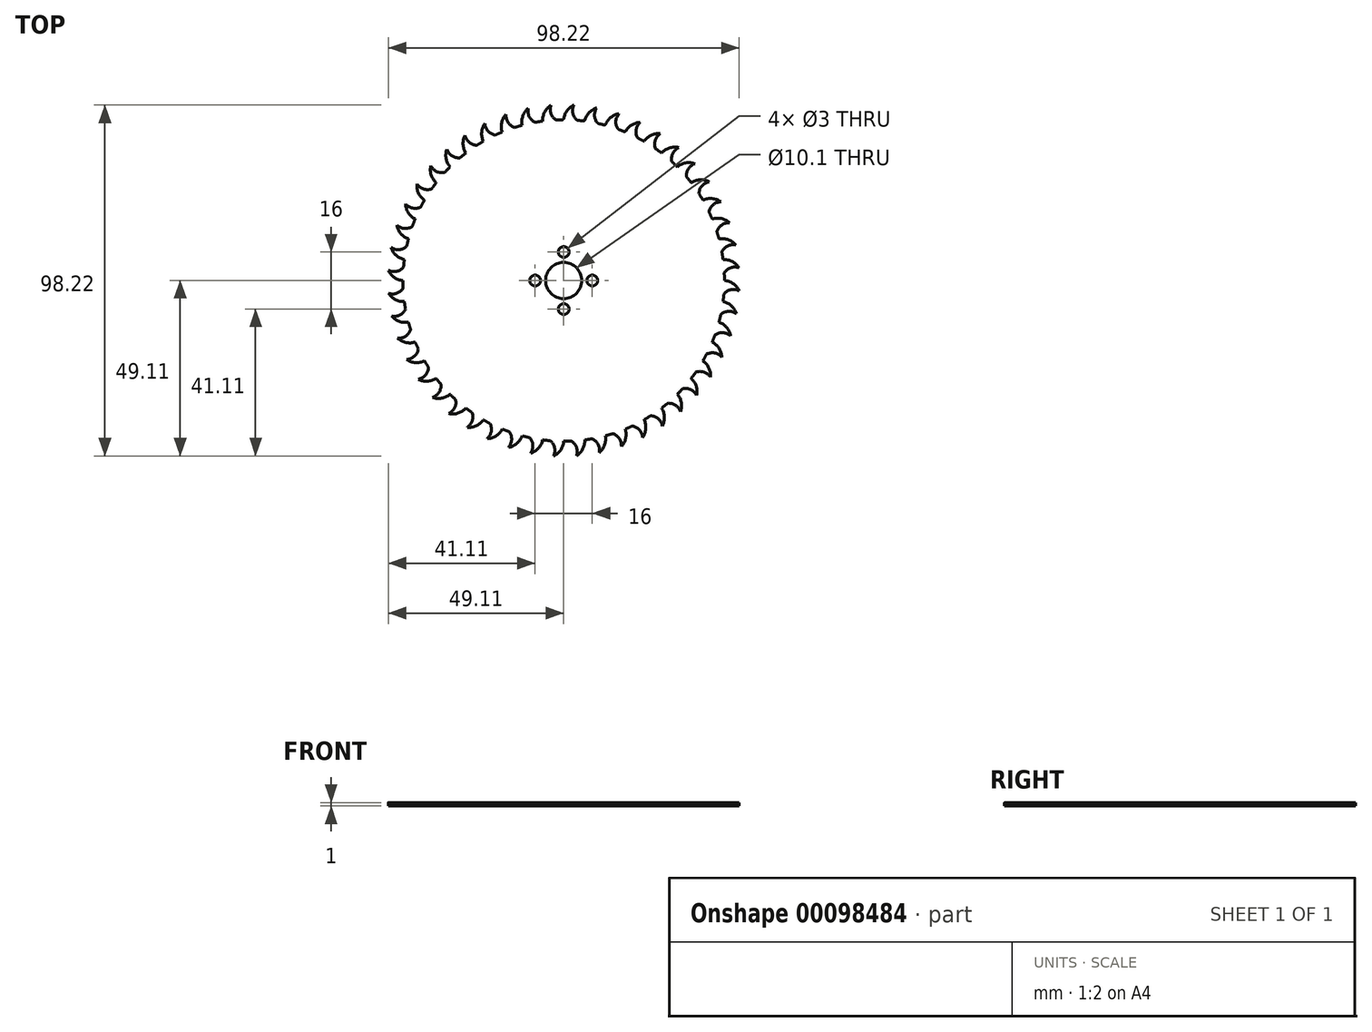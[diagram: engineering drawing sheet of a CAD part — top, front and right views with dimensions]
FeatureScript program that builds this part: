
annotation { "Feature Type Name" : "Feature", "Feature Type Description" : "" }
export const myFeature = defineFeature(function(context is Context, id is Id, definition is map)
    precondition{}
    {
        {
            var Q0;
            Q0=qCreatedBy(makeId("Top.planeOp"),FACE);
            var sketch = newSketch(context, id + "F0", { "sketchPlane" : qUnion([Q0])});
            skCircle(sketch, "E0", {"center": v(0, 0) * mm, "radius": 45 * mm, "construction": true});
            skArc(sketch, "E1", {"start": v(2.87, 49.11) * mm, "mid": v(1, 47.62) * mm, "end": v(0.05, 45.42) * mm});
            skArc(sketch, "E2", {"start": v(2.87, 49.11) * mm, "mid": v(2.52, 47.02) * mm, "end": v(3.45, 45.12) * mm});
            skArc(sketch, "E3.1.0", {"start": v(-3.57, 49.07) * mm, "mid": v(-5.33, 47.15) * mm, "end": v(-5.87, 44.62) * mm});
            skArc(sketch, "E3.1.1", {"start": v(-3.57, 49.07) * mm, "mid": v(-3.64, 46.95) * mm, "end": v(-2.47, 45.19) * mm});
            skArc(sketch, "E3.2.0", {"start": v(-9.94, 48.18) * mm, "mid": v(-11.44, 46.06) * mm, "end": v(-11.65, 43.47) * mm});
            skArc(sketch, "E3.2.1", {"start": v(-9.94, 48.18) * mm, "mid": v(-9.65, 45.9) * mm, "end": v(-8, 44.28) * mm});
            skArc(sketch, "E3.3.0", {"start": v(-16.15, 46.47) * mm, "mid": v(-17.35, 44.17) * mm, "end": v(-17.22, 41.57) * mm});
            skArc(sketch, "E3.3.1", {"start": v(-16.15, 46.47) * mm, "mid": v(-15.56, 44.24) * mm, "end": v(-13.7, 42.86) * mm});
            skArc(sketch, "E3.4.0", {"start": v(-22.07, 43.97) * mm, "mid": v(-22.97, 41.53) * mm, "end": v(-22.5, 38.97) * mm});
            skArc(sketch, "E3.4.1", {"start": v(-22.07, 43.97) * mm, "mid": v(-21.2, 41.83) * mm, "end": v(-19.18, 40.7) * mm});
            skArc(sketch, "E3.5.0", {"start": v(-27.62, 40.7) * mm, "mid": v(-28.2, 38.17) * mm, "end": v(-27.4, 35.7) * mm});
            skArc(sketch, "E3.5.1", {"start": v(-27.62, 40.7) * mm, "mid": v(-26.48, 38.7) * mm, "end": v(-24.33, 37.86) * mm});
            skArc(sketch, "E3.6.0", {"start": v(-32.7, 36.75) * mm, "mid": v(-32.93, 34.17) * mm, "end": v(-31.82, 31.82) * mm});
            skArc(sketch, "E3.6.1", {"start": v(-32.7, 36.75) * mm, "mid": v(-31.3, 34.92) * mm, "end": v(-29.06, 34.36) * mm});
            skArc(sketch, "E3.7.0", {"start": v(-37.22, 32.17) * mm, "mid": v(-37.11, 29.58) * mm, "end": v(-35.7, 27.4) * mm});
            skArc(sketch, "E3.7.1", {"start": v(-37.22, 32.17) * mm, "mid": v(-35.6, 30.53) * mm, "end": v(-33.3, 30.27) * mm});
            skArc(sketch, "E3.8.0", {"start": v(-41.1, 27.04) * mm, "mid": v(-40.65, 24.48) * mm, "end": v(-38.97, 22.5) * mm});
            skArc(sketch, "E3.8.1", {"start": v(-41.1, 27.04) * mm, "mid": v(-39.27, 25.63) * mm, "end": v(-36.96, 25.66) * mm});
            skArc(sketch, "E3.9.0", {"start": v(-44.28, 21.44) * mm, "mid": v(-43.5, 18.96) * mm, "end": v(-41.57, 17.22) * mm});
            skArc(sketch, "E3.9.1", {"start": v(-44.28, 21.44) * mm, "mid": v(-42.28, 20.28) * mm, "end": v(-40, 20.62) * mm});
            skArc(sketch, "E3.10.0", {"start": v(-46.7, 15.48) * mm, "mid": v(-45.6, 13.12) * mm, "end": v(-43.47, 11.65) * mm});
            skArc(sketch, "E3.10.1", {"start": v(-46.7, 15.48) * mm, "mid": v(-44.57, 14.59) * mm, "end": v(-42.35, 15.22) * mm});
            skArc(sketch, "E3.11.0", {"start": v(-48.32, 9.25) * mm, "mid": v(-46.93, 7.06) * mm, "end": v(-44.62, 5.87) * mm});
            skArc(sketch, "E3.11.1", {"start": v(-48.32, 9.25) * mm, "mid": v(-46.09, 8.65) * mm, "end": v(-43.97, 9.56) * mm});
            skArc(sketch, "E3.12.0", {"start": v(-49.11, 2.87) * mm, "mid": v(-47.45, 0.87) * mm, "end": v(-45, 0) * mm});
            skArc(sketch, "E3.12.1", {"start": v(-49.11, 2.87) * mm, "mid": v(-46.82, 2.56) * mm, "end": v(-44.84, 3.74) * mm});
            skArc(sketch, "E3.13.0", {"start": v(-49.07, -3.57) * mm, "mid": v(-47.15, -5.33) * mm, "end": v(-44.62, -5.87) * mm});
            skArc(sketch, "E3.13.1", {"start": v(-49.07, -3.57) * mm, "mid": v(-46.76, -3.58) * mm, "end": v(-44.95, -2.14) * mm});
            skArc(sketch, "E3.14.0", {"start": v(-48.18, -9.94) * mm, "mid": v(-46.06, -11.44) * mm, "end": v(-43.47, -11.65) * mm});
            skArc(sketch, "E3.14.1", {"start": v(-48.18, -9.94) * mm, "mid": v(-45.9, -9.65) * mm, "end": v(-44.28, -8) * mm});
            skArc(sketch, "E3.15.0", {"start": v(-46.47, -16.15) * mm, "mid": v(-44.17, -17.35) * mm, "end": v(-41.57, -17.22) * mm});
            skArc(sketch, "E3.15.1", {"start": v(-46.47, -16.15) * mm, "mid": v(-44.24, -15.56) * mm, "end": v(-42.86, -13.7) * mm});
            skArc(sketch, "E3.16.0", {"start": v(-43.97, -22.07) * mm, "mid": v(-41.53, -22.97) * mm, "end": v(-38.97, -22.5) * mm});
            skArc(sketch, "E3.16.1", {"start": v(-43.97, -22.07) * mm, "mid": v(-41.83, -21.2) * mm, "end": v(-40.7, -19.18) * mm});
            skArc(sketch, "E3.17.0", {"start": v(-40.7, -27.62) * mm, "mid": v(-38.17, -28.2) * mm, "end": v(-35.7, -27.4) * mm});
            skArc(sketch, "E3.17.1", {"start": v(-40.7, -27.62) * mm, "mid": v(-38.7, -26.48) * mm, "end": v(-37.86, -24.33) * mm});
            skArc(sketch, "E3.18.0", {"start": v(-36.75, -32.7) * mm, "mid": v(-34.17, -32.93) * mm, "end": v(-31.82, -31.82) * mm});
            skArc(sketch, "E3.18.1", {"start": v(-36.75, -32.7) * mm, "mid": v(-34.92, -31.3) * mm, "end": v(-34.36, -29.06) * mm});
            skArc(sketch, "E3.19.0", {"start": v(-32.17, -37.22) * mm, "mid": v(-29.58, -37.11) * mm, "end": v(-27.4, -35.7) * mm});
            skArc(sketch, "E3.19.1", {"start": v(-32.17, -37.22) * mm, "mid": v(-30.53, -35.6) * mm, "end": v(-30.27, -33.3) * mm});
            skArc(sketch, "E3.20.0", {"start": v(-27.04, -41.1) * mm, "mid": v(-24.48, -40.65) * mm, "end": v(-22.5, -38.97) * mm});
            skArc(sketch, "E3.20.1", {"start": v(-27.04, -41.1) * mm, "mid": v(-25.63, -39.27) * mm, "end": v(-25.66, -36.96) * mm});
            skArc(sketch, "E3.21.0", {"start": v(-21.44, -44.28) * mm, "mid": v(-18.96, -43.5) * mm, "end": v(-17.22, -41.57) * mm});
            skArc(sketch, "E3.21.1", {"start": v(-21.44, -44.28) * mm, "mid": v(-20.28, -42.28) * mm, "end": v(-20.62, -40) * mm});
            skArc(sketch, "E3.22.0", {"start": v(-15.48, -46.7) * mm, "mid": v(-13.12, -45.6) * mm, "end": v(-11.65, -43.47) * mm});
            skArc(sketch, "E3.22.1", {"start": v(-15.48, -46.7) * mm, "mid": v(-14.59, -44.57) * mm, "end": v(-15.22, -42.35) * mm});
            skArc(sketch, "E3.23.0", {"start": v(-9.25, -48.32) * mm, "mid": v(-7.06, -46.93) * mm, "end": v(-5.87, -44.62) * mm});
            skArc(sketch, "E3.23.1", {"start": v(-9.25, -48.32) * mm, "mid": v(-8.65, -46.09) * mm, "end": v(-9.56, -43.97) * mm});
            skArc(sketch, "E3.24.0", {"start": v(-2.87, -49.11) * mm, "mid": v(-0.87, -47.45) * mm, "end": v(0, -45) * mm});
            skArc(sketch, "E3.24.1", {"start": v(-2.87, -49.11) * mm, "mid": v(-2.56, -46.82) * mm, "end": v(-3.74, -44.84) * mm});
            skArc(sketch, "E3.25.0", {"start": v(3.57, -49.07) * mm, "mid": v(5.33, -47.15) * mm, "end": v(5.87, -44.62) * mm});
            skArc(sketch, "E3.25.1", {"start": v(3.57, -49.07) * mm, "mid": v(3.58, -46.76) * mm, "end": v(2.14, -44.95) * mm});
            skArc(sketch, "E3.26.0", {"start": v(9.94, -48.18) * mm, "mid": v(11.44, -46.06) * mm, "end": v(11.65, -43.47) * mm});
            skArc(sketch, "E3.26.1", {"start": v(9.94, -48.18) * mm, "mid": v(9.65, -45.9) * mm, "end": v(8, -44.28) * mm});
            skArc(sketch, "E3.27.0", {"start": v(16.15, -46.47) * mm, "mid": v(17.35, -44.17) * mm, "end": v(17.22, -41.57) * mm});
            skArc(sketch, "E3.27.1", {"start": v(16.15, -46.47) * mm, "mid": v(15.56, -44.24) * mm, "end": v(13.7, -42.86) * mm});
            skArc(sketch, "E3.28.0", {"start": v(22.07, -43.97) * mm, "mid": v(22.97, -41.53) * mm, "end": v(22.5, -38.97) * mm});
            skArc(sketch, "E3.28.1", {"start": v(22.07, -43.97) * mm, "mid": v(21.2, -41.83) * mm, "end": v(19.18, -40.7) * mm});
            skArc(sketch, "E3.29.0", {"start": v(27.62, -40.7) * mm, "mid": v(28.2, -38.17) * mm, "end": v(27.4, -35.7) * mm});
            skArc(sketch, "E3.29.1", {"start": v(27.62, -40.7) * mm, "mid": v(26.48, -38.7) * mm, "end": v(24.33, -37.86) * mm});
            skArc(sketch, "E3.30.0", {"start": v(32.7, -36.75) * mm, "mid": v(32.93, -34.17) * mm, "end": v(31.82, -31.82) * mm});
            skArc(sketch, "E3.30.1", {"start": v(32.7, -36.75) * mm, "mid": v(31.3, -34.92) * mm, "end": v(29.06, -34.36) * mm});
            skArc(sketch, "E3.31.0", {"start": v(37.22, -32.17) * mm, "mid": v(37.11, -29.58) * mm, "end": v(35.7, -27.4) * mm});
            skArc(sketch, "E3.31.1", {"start": v(37.22, -32.17) * mm, "mid": v(35.6, -30.53) * mm, "end": v(33.3, -30.27) * mm});
            skArc(sketch, "E3.32.0", {"start": v(41.1, -27.04) * mm, "mid": v(40.65, -24.48) * mm, "end": v(38.97, -22.5) * mm});
            skArc(sketch, "E3.32.1", {"start": v(41.1, -27.04) * mm, "mid": v(39.27, -25.63) * mm, "end": v(36.96, -25.66) * mm});
            skArc(sketch, "E3.33.0", {"start": v(44.28, -21.44) * mm, "mid": v(43.5, -18.96) * mm, "end": v(41.57, -17.22) * mm});
            skArc(sketch, "E3.33.1", {"start": v(44.28, -21.44) * mm, "mid": v(42.28, -20.28) * mm, "end": v(40, -20.62) * mm});
            skArc(sketch, "E3.34.0", {"start": v(46.7, -15.48) * mm, "mid": v(45.6, -13.12) * mm, "end": v(43.47, -11.65) * mm});
            skArc(sketch, "E3.34.1", {"start": v(46.7, -15.48) * mm, "mid": v(44.57, -14.59) * mm, "end": v(42.35, -15.22) * mm});
            skArc(sketch, "E3.35.0", {"start": v(48.32, -9.25) * mm, "mid": v(46.93, -7.06) * mm, "end": v(44.62, -5.87) * mm});
            skArc(sketch, "E3.35.1", {"start": v(48.32, -9.25) * mm, "mid": v(46.09, -8.65) * mm, "end": v(43.97, -9.56) * mm});
            skArc(sketch, "E3.36.0", {"start": v(49.11, -2.87) * mm, "mid": v(47.45, -0.87) * mm, "end": v(45, 0) * mm});
            skArc(sketch, "E3.36.1", {"start": v(49.11, -2.87) * mm, "mid": v(46.82, -2.56) * mm, "end": v(44.84, -3.74) * mm});
            skArc(sketch, "E3.37.0", {"start": v(49.07, 3.57) * mm, "mid": v(47.15, 5.33) * mm, "end": v(44.62, 5.87) * mm});
            skArc(sketch, "E3.37.1", {"start": v(49.07, 3.57) * mm, "mid": v(46.76, 3.58) * mm, "end": v(44.95, 2.14) * mm});
            skArc(sketch, "E3.38.0", {"start": v(48.18, 9.94) * mm, "mid": v(46.06, 11.44) * mm, "end": v(43.47, 11.65) * mm});
            skArc(sketch, "E3.38.1", {"start": v(48.18, 9.94) * mm, "mid": v(45.9, 9.65) * mm, "end": v(44.28, 8) * mm});
            skArc(sketch, "E3.39.0", {"start": v(46.47, 16.15) * mm, "mid": v(44.17, 17.35) * mm, "end": v(41.57, 17.22) * mm});
            skArc(sketch, "E3.39.1", {"start": v(46.47, 16.15) * mm, "mid": v(44.24, 15.56) * mm, "end": v(42.86, 13.7) * mm});
            skArc(sketch, "E3.40.0", {"start": v(43.97, 22.07) * mm, "mid": v(41.53, 22.97) * mm, "end": v(38.97, 22.5) * mm});
            skArc(sketch, "E3.40.1", {"start": v(43.97, 22.07) * mm, "mid": v(41.83, 21.2) * mm, "end": v(40.7, 19.18) * mm});
            skArc(sketch, "E3.41.0", {"start": v(40.7, 27.62) * mm, "mid": v(38.17, 28.2) * mm, "end": v(35.7, 27.4) * mm});
            skArc(sketch, "E3.41.1", {"start": v(40.7, 27.62) * mm, "mid": v(38.7, 26.48) * mm, "end": v(37.86, 24.33) * mm});
            skArc(sketch, "E3.42.0", {"start": v(36.75, 32.7) * mm, "mid": v(34.17, 32.93) * mm, "end": v(31.82, 31.82) * mm});
            skArc(sketch, "E3.42.1", {"start": v(36.75, 32.7) * mm, "mid": v(34.92, 31.3) * mm, "end": v(34.36, 29.06) * mm});
            skArc(sketch, "E3.43.0", {"start": v(32.17, 37.22) * mm, "mid": v(29.58, 37.11) * mm, "end": v(27.4, 35.7) * mm});
            skArc(sketch, "E3.43.1", {"start": v(32.17, 37.22) * mm, "mid": v(30.53, 35.6) * mm, "end": v(30.27, 33.3) * mm});
            skArc(sketch, "E3.44.0", {"start": v(27.04, 41.1) * mm, "mid": v(24.48, 40.65) * mm, "end": v(22.5, 38.97) * mm});
            skArc(sketch, "E3.44.1", {"start": v(27.04, 41.1) * mm, "mid": v(25.63, 39.27) * mm, "end": v(25.66, 36.96) * mm});
            skArc(sketch, "E3.45.0", {"start": v(21.44, 44.28) * mm, "mid": v(19.14, 43.61) * mm, "end": v(17.43, 41.94) * mm});
            skArc(sketch, "E3.45.1", {"start": v(21.44, 44.28) * mm, "mid": v(20.28, 42.28) * mm, "end": v(20.62, 40) * mm});
            skArc(sketch, "E3.46.0", {"start": v(15.48, 46.7) * mm, "mid": v(13.29, 45.74) * mm, "end": v(11.8, 43.86) * mm});
            skArc(sketch, "E3.46.1", {"start": v(15.48, 46.7) * mm, "mid": v(14.6, 44.77) * mm, "end": v(15, 42.7) * mm});
            skArc(sketch, "E3.47.0", {"start": v(9.25, 48.32) * mm, "mid": v(7.2, 47.08) * mm, "end": v(5.98, 45.02) * mm});
            skArc(sketch, "E3.47.1", {"start": v(9.25, 48.32) * mm, "mid": v(8.64, 46.3) * mm, "end": v(9.3, 44.29) * mm});
            skArc(sketch, "E4", {"start": v(4.08, 44.81) * mm, "mid": v(4.76, 44.75) * mm, "end": v(5.44, 44.67) * mm});
            skArc(sketch, "E5.1.0", {"start": v(-1.8, 44.96) * mm, "mid": v(-1.12, 44.99) * mm, "end": v(-0.44, 45) * mm});
            skArc(sketch, "E5.2.0", {"start": v(-8, 44.28) * mm, "mid": v(-6.93, 44.46) * mm, "end": v(-5.87, 44.62) * mm});
            skArc(sketch, "E5.3.0", {"start": v(-13.7, 42.86) * mm, "mid": v(-12.68, 43.18) * mm, "end": v(-11.65, 43.47) * mm});
            skArc(sketch, "E5.4.0", {"start": v(-19.18, 40.7) * mm, "mid": v(-18.2, 41.15) * mm, "end": v(-17.22, 41.57) * mm});
            skArc(sketch, "E5.5.0", {"start": v(-24.33, 37.86) * mm, "mid": v(-23.42, 38.42) * mm, "end": v(-22.5, 38.97) * mm});
            skArc(sketch, "E5.6.0", {"start": v(-29.06, 34.36) * mm, "mid": v(-28.24, 35.04) * mm, "end": v(-27.4, 35.7) * mm});
            skArc(sketch, "E5.7.0", {"start": v(-33.3, 30.27) * mm, "mid": v(-32.57, 31.05) * mm, "end": v(-31.82, 31.82) * mm});
            skArc(sketch, "E5.8.0", {"start": v(-36.96, 25.66) * mm, "mid": v(-36.34, 26.54) * mm, "end": v(-35.7, 27.4) * mm});
            skArc(sketch, "E5.9.0", {"start": v(-40, 20.62) * mm, "mid": v(-39.5, 21.57) * mm, "end": v(-38.97, 22.5) * mm});
            skArc(sketch, "E5.10.0", {"start": v(-42.35, 15.22) * mm, "mid": v(-41.97, 16.23) * mm, "end": v(-41.57, 17.22) * mm});
            skArc(sketch, "E5.11.0", {"start": v(-43.97, 9.56) * mm, "mid": v(-43.73, 10.6) * mm, "end": v(-43.47, 11.65) * mm});
            skArc(sketch, "E5.12.0", {"start": v(-44.84, 3.74) * mm, "mid": v(-44.74, 4.8) * mm, "end": v(-44.62, 5.87) * mm});
            skArc(sketch, "E5.13.0", {"start": v(-44.95, -2.14) * mm, "mid": v(-44.99, -1.07) * mm, "end": v(-45, 0) * mm});
            skArc(sketch, "E5.14.0", {"start": v(-44.28, -8) * mm, "mid": v(-44.46, -6.93) * mm, "end": v(-44.62, -5.87) * mm});
            skArc(sketch, "E5.15.0", {"start": v(-42.86, -13.7) * mm, "mid": v(-43.18, -12.68) * mm, "end": v(-43.47, -11.65) * mm});
            skArc(sketch, "E5.16.0", {"start": v(-40.7, -19.18) * mm, "mid": v(-41.15, -18.2) * mm, "end": v(-41.57, -17.22) * mm});
            skArc(sketch, "E5.17.0", {"start": v(-37.86, -24.33) * mm, "mid": v(-38.42, -23.42) * mm, "end": v(-38.97, -22.5) * mm});
            skArc(sketch, "E5.18.0", {"start": v(-34.36, -29.06) * mm, "mid": v(-35.04, -28.24) * mm, "end": v(-35.7, -27.4) * mm});
            skArc(sketch, "E5.19.0", {"start": v(-30.27, -33.3) * mm, "mid": v(-31.05, -32.57) * mm, "end": v(-31.82, -31.82) * mm});
            skArc(sketch, "E5.20.0", {"start": v(-25.66, -36.96) * mm, "mid": v(-26.54, -36.34) * mm, "end": v(-27.4, -35.7) * mm});
            skArc(sketch, "E5.21.0", {"start": v(-20.62, -40) * mm, "mid": v(-21.57, -39.5) * mm, "end": v(-22.5, -38.97) * mm});
            skArc(sketch, "E5.22.0", {"start": v(-15.22, -42.35) * mm, "mid": v(-16.23, -41.97) * mm, "end": v(-17.22, -41.57) * mm});
            skArc(sketch, "E5.23.0", {"start": v(-9.56, -43.97) * mm, "mid": v(-10.6, -43.73) * mm, "end": v(-11.65, -43.47) * mm});
            skArc(sketch, "E5.24.0", {"start": v(-3.74, -44.84) * mm, "mid": v(-4.8, -44.74) * mm, "end": v(-5.87, -44.62) * mm});
            skArc(sketch, "E5.25.0", {"start": v(2.14, -44.95) * mm, "mid": v(1.07, -44.99) * mm, "end": v(0, -45) * mm});
            skArc(sketch, "E5.26.0", {"start": v(8, -44.28) * mm, "mid": v(6.93, -44.46) * mm, "end": v(5.87, -44.62) * mm});
            skArc(sketch, "E5.27.0", {"start": v(13.7, -42.86) * mm, "mid": v(12.68, -43.18) * mm, "end": v(11.65, -43.47) * mm});
            skArc(sketch, "E5.28.0", {"start": v(19.18, -40.7) * mm, "mid": v(18.2, -41.15) * mm, "end": v(17.22, -41.57) * mm});
            skArc(sketch, "E5.29.0", {"start": v(24.33, -37.86) * mm, "mid": v(23.42, -38.42) * mm, "end": v(22.5, -38.97) * mm});
            skArc(sketch, "E5.30.0", {"start": v(29.06, -34.36) * mm, "mid": v(28.24, -35.04) * mm, "end": v(27.4, -35.7) * mm});
            skArc(sketch, "E5.31.0", {"start": v(33.3, -30.27) * mm, "mid": v(32.57, -31.05) * mm, "end": v(31.82, -31.82) * mm});
            skArc(sketch, "E5.32.0", {"start": v(36.96, -25.66) * mm, "mid": v(36.34, -26.54) * mm, "end": v(35.7, -27.4) * mm});
            skArc(sketch, "E5.33.0", {"start": v(40, -20.62) * mm, "mid": v(39.5, -21.57) * mm, "end": v(38.97, -22.5) * mm});
            skArc(sketch, "E5.34.0", {"start": v(42.35, -15.22) * mm, "mid": v(41.97, -16.23) * mm, "end": v(41.57, -17.22) * mm});
            skArc(sketch, "E5.35.0", {"start": v(43.97, -9.56) * mm, "mid": v(43.73, -10.6) * mm, "end": v(43.47, -11.65) * mm});
            skArc(sketch, "E5.36.0", {"start": v(44.84, -3.74) * mm, "mid": v(44.74, -4.8) * mm, "end": v(44.62, -5.87) * mm});
            skArc(sketch, "E5.37.0", {"start": v(44.95, 2.14) * mm, "mid": v(44.99, 1.07) * mm, "end": v(45, 0) * mm});
            skArc(sketch, "E5.38.0", {"start": v(44.28, 8) * mm, "mid": v(44.46, 6.93) * mm, "end": v(44.62, 5.87) * mm});
            skArc(sketch, "E5.39.0", {"start": v(42.86, 13.7) * mm, "mid": v(43.18, 12.68) * mm, "end": v(43.47, 11.65) * mm});
            skArc(sketch, "E5.40.0", {"start": v(40.7, 19.18) * mm, "mid": v(41.15, 18.2) * mm, "end": v(41.57, 17.22) * mm});
            skArc(sketch, "E5.41.0", {"start": v(37.86, 24.33) * mm, "mid": v(38.42, 23.42) * mm, "end": v(38.97, 22.5) * mm});
            skArc(sketch, "E5.42.0", {"start": v(34.36, 29.06) * mm, "mid": v(35.04, 28.24) * mm, "end": v(35.7, 27.4) * mm});
            skArc(sketch, "E5.43.0", {"start": v(30.27, 33.3) * mm, "mid": v(31.05, 32.57) * mm, "end": v(31.82, 31.82) * mm});
            skArc(sketch, "E5.44.0", {"start": v(25.66, 36.96) * mm, "mid": v(26.54, 36.34) * mm, "end": v(27.4, 35.7) * mm});
            skArc(sketch, "E5.45.0", {"start": v(20.62, 40) * mm, "mid": v(21.57, 39.5) * mm, "end": v(22.5, 38.97) * mm});
            skArc(sketch, "E5.46.0", {"start": v(15.54, 42.23) * mm, "mid": v(16.18, 42) * mm, "end": v(16.81, 41.74) * mm});
            skArc(sketch, "E5.47.0", {"start": v(9.9, 43.9) * mm, "mid": v(10.56, 43.74) * mm, "end": v(11.22, 43.58) * mm});
            skPoint(sketch, "E6.visualSharp", {"position": v(9.56, 43.97) * mm});
            skArc(sketch, "E6.filletArc", {"start": v(9.3, 44.29) * mm, "mid": v(9.57, 44.04) * mm, "end": v(9.9, 43.9) * mm});
            skPoint(sketch, "E7.visualSharp", {"position": v(11.65, 43.47) * mm});
            skArc(sketch, "E7.filletArc", {"start": v(11.22, 43.58) * mm, "mid": v(11.56, 43.61) * mm, "end": v(11.8, 43.86) * mm});
            skPoint(sketch, "E8.visualSharp", {"position": v(3.74, 44.84) * mm});
            skArc(sketch, "E8.filletArc", {"start": v(3.45, 45.12) * mm, "mid": v(3.74, 44.91) * mm, "end": v(4.08, 44.81) * mm});
            skPoint(sketch, "E9.visualSharp", {"position": v(-2.14, 44.95) * mm});
            skArc(sketch, "E9.filletArc", {"start": v(-2.47, 45.19) * mm, "mid": v(-2.16, 45.01) * mm, "end": v(-1.8, 44.96) * mm});
            skPoint(sketch, "E10.visualSharp", {"position": v(0, 45) * mm});
            skArc(sketch, "E10.filletArc", {"start": v(-0.44, 45) * mm, "mid": v(-0.12, 45.12) * mm, "end": v(0.05, 45.42) * mm});
            skPoint(sketch, "E11.visualSharp", {"position": v(5.87, 44.62) * mm});
            skArc(sketch, "E11.filletArc", {"start": v(5.44, 44.67) * mm, "mid": v(5.77, 44.75) * mm, "end": v(5.98, 45.02) * mm});
            skPoint(sketch, "E12.visualSharp", {"position": v(17.22, 41.57) * mm});
            skArc(sketch, "E12.filletArc", {"start": v(16.81, 41.74) * mm, "mid": v(17.16, 41.73) * mm, "end": v(17.43, 41.94) * mm});
            skPoint(sketch, "E13.visualSharp", {"position": v(15.22, 42.35) * mm});
            skArc(sketch, "E13.filletArc", {"start": v(15, 42.7) * mm, "mid": v(15.23, 42.41) * mm, "end": v(15.54, 42.23) * mm});
            skCircle(sketch, "E14", {"center": v(0, 0) * mm, "radius": 5.05 * mm});
            skSolve(sketch);
        }
        {
            var Q0;
            Q0=qSketchRegion(id+"F0",true);
            extrude(context, id + "F1", {"entities" : qUnion([Q0]), "depth" : 1 * mm});
        }
        {
            var Q0;
            Q0=makeQuery(id+"F1.opExtrude","CAP_FACE",FACE,{"disambiguationData":[OSD([sQuery(id+"F0.wireOp",EDGE,"E1"),sQuery(id+"F0.wireOp",EDGE,"E2"),sQuery(id+"F0.wireOp",EDGE,"E3.1.0"),sQuery(id+"F0.wireOp",EDGE,"E3.1.1"),sQuery(id+"F0.wireOp",EDGE,"E3.2.0"),sQuery(id+"F0.wireOp",EDGE,"E3.2.1"),sQuery(id+"F0.wireOp",EDGE,"E3.3.0"),sQuery(id+"F0.wireOp",EDGE,"E3.3.1"),sQuery(id+"F0.wireOp",EDGE,"E3.4.0"),sQuery(id+"F0.wireOp",EDGE,"E3.4.1"),sQuery(id+"F0.wireOp",EDGE,"E3.5.0"),sQuery(id+"F0.wireOp",EDGE,"E3.5.1"),sQuery(id+"F0.wireOp",EDGE,"E3.6.0"),sQuery(id+"F0.wireOp",EDGE,"E3.6.1"),sQuery(id+"F0.wireOp",EDGE,"E3.7.0"),sQuery(id+"F0.wireOp",EDGE,"E3.7.1"),sQuery(id+"F0.wireOp",EDGE,"E3.8.0"),sQuery(id+"F0.wireOp",EDGE,"E3.8.1"),sQuery(id+"F0.wireOp",EDGE,"E3.9.0"),sQuery(id+"F0.wireOp",EDGE,"E3.9.1"),sQuery(id+"F0.wireOp",EDGE,"E3.10.0"),sQuery(id+"F0.wireOp",EDGE,"E3.10.1"),sQuery(id+"F0.wireOp",EDGE,"E3.11.0"),sQuery(id+"F0.wireOp",EDGE,"E3.11.1"),sQuery(id+"F0.wireOp",EDGE,"E3.12.0"),sQuery(id+"F0.wireOp",EDGE,"E3.12.1"),sQuery(id+"F0.wireOp",EDGE,"E3.13.0"),sQuery(id+"F0.wireOp",EDGE,"E3.13.1"),sQuery(id+"F0.wireOp",EDGE,"E3.14.0"),sQuery(id+"F0.wireOp",EDGE,"E3.14.1"),sQuery(id+"F0.wireOp",EDGE,"E3.15.0"),sQuery(id+"F0.wireOp",EDGE,"E3.15.1"),sQuery(id+"F0.wireOp",EDGE,"E3.16.0"),sQuery(id+"F0.wireOp",EDGE,"E3.16.1"),sQuery(id+"F0.wireOp",EDGE,"E3.17.0"),sQuery(id+"F0.wireOp",EDGE,"E3.17.1"),sQuery(id+"F0.wireOp",EDGE,"E3.18.0"),sQuery(id+"F0.wireOp",EDGE,"E3.18.1"),sQuery(id+"F0.wireOp",EDGE,"E3.19.0"),sQuery(id+"F0.wireOp",EDGE,"E3.19.1"),sQuery(id+"F0.wireOp",EDGE,"E3.20.0"),sQuery(id+"F0.wireOp",EDGE,"E3.20.1"),sQuery(id+"F0.wireOp",EDGE,"E3.21.0"),sQuery(id+"F0.wireOp",EDGE,"E3.21.1"),sQuery(id+"F0.wireOp",EDGE,"E3.22.0"),sQuery(id+"F0.wireOp",EDGE,"E3.22.1"),sQuery(id+"F0.wireOp",EDGE,"E3.23.0"),sQuery(id+"F0.wireOp",EDGE,"E3.23.1"),sQuery(id+"F0.wireOp",EDGE,"E3.24.0"),sQuery(id+"F0.wireOp",EDGE,"E3.24.1"),sQuery(id+"F0.wireOp",EDGE,"E3.25.0"),sQuery(id+"F0.wireOp",EDGE,"E3.25.1"),sQuery(id+"F0.wireOp",EDGE,"E3.26.0"),sQuery(id+"F0.wireOp",EDGE,"E3.26.1"),sQuery(id+"F0.wireOp",EDGE,"E3.27.0"),sQuery(id+"F0.wireOp",EDGE,"E3.27.1"),sQuery(id+"F0.wireOp",EDGE,"E3.28.0"),sQuery(id+"F0.wireOp",EDGE,"E3.28.1"),sQuery(id+"F0.wireOp",EDGE,"E3.29.0"),sQuery(id+"F0.wireOp",EDGE,"E3.29.1"),sQuery(id+"F0.wireOp",EDGE,"E3.30.0"),sQuery(id+"F0.wireOp",EDGE,"E3.30.1"),sQuery(id+"F0.wireOp",EDGE,"E3.31.0"),sQuery(id+"F0.wireOp",EDGE,"E3.31.1"),sQuery(id+"F0.wireOp",EDGE,"E3.32.0"),sQuery(id+"F0.wireOp",EDGE,"E3.32.1"),sQuery(id+"F0.wireOp",EDGE,"E3.33.0"),sQuery(id+"F0.wireOp",EDGE,"E3.33.1"),sQuery(id+"F0.wireOp",EDGE,"E3.34.0"),sQuery(id+"F0.wireOp",EDGE,"E3.34.1"),sQuery(id+"F0.wireOp",EDGE,"E3.35.0"),sQuery(id+"F0.wireOp",EDGE,"E3.35.1"),sQuery(id+"F0.wireOp",EDGE,"E3.36.0"),sQuery(id+"F0.wireOp",EDGE,"E3.36.1"),sQuery(id+"F0.wireOp",EDGE,"E3.37.0"),sQuery(id+"F0.wireOp",EDGE,"E3.37.1"),sQuery(id+"F0.wireOp",EDGE,"E3.38.0"),sQuery(id+"F0.wireOp",EDGE,"E3.38.1"),sQuery(id+"F0.wireOp",EDGE,"E3.39.0"),sQuery(id+"F0.wireOp",EDGE,"E3.39.1"),sQuery(id+"F0.wireOp",EDGE,"E3.40.0"),sQuery(id+"F0.wireOp",EDGE,"E3.40.1"),sQuery(id+"F0.wireOp",EDGE,"E3.41.0"),sQuery(id+"F0.wireOp",EDGE,"E3.41.1"),sQuery(id+"F0.wireOp",EDGE,"E3.42.0"),sQuery(id+"F0.wireOp",EDGE,"E3.42.1"),sQuery(id+"F0.wireOp",EDGE,"E3.43.0"),sQuery(id+"F0.wireOp",EDGE,"E3.43.1"),sQuery(id+"F0.wireOp",EDGE,"E3.44.0"),sQuery(id+"F0.wireOp",EDGE,"E3.44.1"),sQuery(id+"F0.wireOp",EDGE,"E3.45.0"),sQuery(id+"F0.wireOp",EDGE,"E3.45.1"),sQuery(id+"F0.wireOp",EDGE,"E3.46.0"),sQuery(id+"F0.wireOp",EDGE,"E3.46.1"),sQuery(id+"F0.wireOp",EDGE,"E3.47.0"),sQuery(id+"F0.wireOp",EDGE,"E3.47.1"),sQuery(id+"F0.wireOp",EDGE,"E4"),sQuery(id+"F0.wireOp",EDGE,"E5.1.0"),sQuery(id+"F0.wireOp",EDGE,"E5.2.0"),sQuery(id+"F0.wireOp",EDGE,"E5.3.0"),sQuery(id+"F0.wireOp",EDGE,"E5.4.0"),sQuery(id+"F0.wireOp",EDGE,"E5.5.0"),sQuery(id+"F0.wireOp",EDGE,"E5.6.0"),sQuery(id+"F0.wireOp",EDGE,"E5.7.0"),sQuery(id+"F0.wireOp",EDGE,"E5.8.0"),sQuery(id+"F0.wireOp",EDGE,"E5.9.0"),sQuery(id+"F0.wireOp",EDGE,"E5.10.0"),sQuery(id+"F0.wireOp",EDGE,"E5.11.0"),sQuery(id+"F0.wireOp",EDGE,"E5.12.0"),sQuery(id+"F0.wireOp",EDGE,"E5.13.0"),sQuery(id+"F0.wireOp",EDGE,"E5.14.0"),sQuery(id+"F0.wireOp",EDGE,"E5.15.0"),sQuery(id+"F0.wireOp",EDGE,"E5.16.0"),sQuery(id+"F0.wireOp",EDGE,"E5.17.0"),sQuery(id+"F0.wireOp",EDGE,"E5.18.0"),sQuery(id+"F0.wireOp",EDGE,"E5.19.0"),sQuery(id+"F0.wireOp",EDGE,"E5.20.0"),sQuery(id+"F0.wireOp",EDGE,"E5.21.0"),sQuery(id+"F0.wireOp",EDGE,"E5.22.0"),sQuery(id+"F0.wireOp",EDGE,"E5.23.0"),sQuery(id+"F0.wireOp",EDGE,"E5.24.0"),sQuery(id+"F0.wireOp",EDGE,"E5.25.0"),sQuery(id+"F0.wireOp",EDGE,"E5.26.0"),sQuery(id+"F0.wireOp",EDGE,"E5.27.0"),sQuery(id+"F0.wireOp",EDGE,"E5.28.0"),sQuery(id+"F0.wireOp",EDGE,"E5.29.0"),sQuery(id+"F0.wireOp",EDGE,"E5.30.0"),sQuery(id+"F0.wireOp",EDGE,"E5.31.0"),sQuery(id+"F0.wireOp",EDGE,"E5.32.0"),sQuery(id+"F0.wireOp",EDGE,"E5.33.0"),sQuery(id+"F0.wireOp",EDGE,"E5.34.0"),sQuery(id+"F0.wireOp",EDGE,"E5.35.0"),sQuery(id+"F0.wireOp",EDGE,"E5.36.0"),sQuery(id+"F0.wireOp",EDGE,"E5.37.0"),sQuery(id+"F0.wireOp",EDGE,"E5.38.0"),sQuery(id+"F0.wireOp",EDGE,"E5.39.0"),sQuery(id+"F0.wireOp",EDGE,"E5.40.0"),sQuery(id+"F0.wireOp",EDGE,"E5.41.0"),sQuery(id+"F0.wireOp",EDGE,"E5.42.0"),sQuery(id+"F0.wireOp",EDGE,"E5.43.0"),sQuery(id+"F0.wireOp",EDGE,"E5.44.0"),sQuery(id+"F0.wireOp",EDGE,"E5.45.0"),sQuery(id+"F0.wireOp",EDGE,"E5.46.0"),sQuery(id+"F0.wireOp",EDGE,"E5.47.0"),sQuery(id+"F0.wireOp",EDGE,"E6.filletArc"),sQuery(id+"F0.wireOp",EDGE,"E7.filletArc"),sQuery(id+"F0.wireOp",EDGE,"E8.filletArc"),sQuery(id+"F0.wireOp",EDGE,"E9.filletArc"),sQuery(id+"F0.wireOp",EDGE,"E10.filletArc"),sQuery(id+"F0.wireOp",EDGE,"E11.filletArc"),sQuery(id+"F0.wireOp",EDGE,"E12.filletArc"),sQuery(id+"F0.wireOp",EDGE,"E13.filletArc"),sQuery(id+"F0.wireOp",EDGE,"E14")])],"isStart":false});
            var sketch = newSketch(context, id + "F2", { "sketchPlane" : qUnion([Q0])});
            skCircle(sketch, "E15", {"center": v(0, 0) * mm, "radius": 8 * mm, "construction": true});
            skPoint(sketch, "E16", {"position": v(0, 8) * mm});
            skPoint(sketch, "E17", {"position": v(-8, 0) * mm});
            skPoint(sketch, "E18", {"position": v(0, -8) * mm});
            skPoint(sketch, "E19", {"position": v(8, 0) * mm});
            skSolve(sketch);
        }
        {
            var Q0;
            Q0=sQuery(id+"F2.wireOp",VERTEX,"E16");
            var Q1;
            Q1=sQuery(id+"F2.wireOp",VERTEX,"E17");
            var Q2;
            Q2=sQuery(id+"F2.wireOp",VERTEX,"E18");
            var Q3;
            Q3=sQuery(id+"F2.wireOp",VERTEX,"E19");
            var Q4;
            Q4=makeQuery(id+"F1.opExtrude","SWEPT_BODY",BODY,{"disambiguationData":[OSD([sQuery(id+"F0.wireOp",EDGE,"E1"),sQuery(id+"F0.wireOp",EDGE,"E2"),sQuery(id+"F0.wireOp",EDGE,"E3.1.0"),sQuery(id+"F0.wireOp",EDGE,"E3.1.1"),sQuery(id+"F0.wireOp",EDGE,"E3.2.0"),sQuery(id+"F0.wireOp",EDGE,"E3.2.1"),sQuery(id+"F0.wireOp",EDGE,"E3.3.0"),sQuery(id+"F0.wireOp",EDGE,"E3.3.1"),sQuery(id+"F0.wireOp",EDGE,"E3.4.0"),sQuery(id+"F0.wireOp",EDGE,"E3.4.1"),sQuery(id+"F0.wireOp",EDGE,"E3.5.0"),sQuery(id+"F0.wireOp",EDGE,"E3.5.1"),sQuery(id+"F0.wireOp",EDGE,"E3.6.0"),sQuery(id+"F0.wireOp",EDGE,"E3.6.1"),sQuery(id+"F0.wireOp",EDGE,"E3.7.0"),sQuery(id+"F0.wireOp",EDGE,"E3.7.1"),sQuery(id+"F0.wireOp",EDGE,"E3.8.0"),sQuery(id+"F0.wireOp",EDGE,"E3.8.1"),sQuery(id+"F0.wireOp",EDGE,"E3.9.0"),sQuery(id+"F0.wireOp",EDGE,"E3.9.1"),sQuery(id+"F0.wireOp",EDGE,"E3.10.0"),sQuery(id+"F0.wireOp",EDGE,"E3.10.1"),sQuery(id+"F0.wireOp",EDGE,"E3.11.0"),sQuery(id+"F0.wireOp",EDGE,"E3.11.1"),sQuery(id+"F0.wireOp",EDGE,"E3.12.0"),sQuery(id+"F0.wireOp",EDGE,"E3.12.1"),sQuery(id+"F0.wireOp",EDGE,"E3.13.0"),sQuery(id+"F0.wireOp",EDGE,"E3.13.1"),sQuery(id+"F0.wireOp",EDGE,"E3.14.0"),sQuery(id+"F0.wireOp",EDGE,"E3.14.1"),sQuery(id+"F0.wireOp",EDGE,"E3.15.0"),sQuery(id+"F0.wireOp",EDGE,"E3.15.1"),sQuery(id+"F0.wireOp",EDGE,"E3.16.0"),sQuery(id+"F0.wireOp",EDGE,"E3.16.1"),sQuery(id+"F0.wireOp",EDGE,"E3.17.0"),sQuery(id+"F0.wireOp",EDGE,"E3.17.1"),sQuery(id+"F0.wireOp",EDGE,"E3.18.0"),sQuery(id+"F0.wireOp",EDGE,"E3.18.1"),sQuery(id+"F0.wireOp",EDGE,"E3.19.0"),sQuery(id+"F0.wireOp",EDGE,"E3.19.1"),sQuery(id+"F0.wireOp",EDGE,"E3.20.0"),sQuery(id+"F0.wireOp",EDGE,"E3.20.1"),sQuery(id+"F0.wireOp",EDGE,"E3.21.0"),sQuery(id+"F0.wireOp",EDGE,"E3.21.1"),sQuery(id+"F0.wireOp",EDGE,"E3.22.0"),sQuery(id+"F0.wireOp",EDGE,"E3.22.1"),sQuery(id+"F0.wireOp",EDGE,"E3.23.0"),sQuery(id+"F0.wireOp",EDGE,"E3.23.1"),sQuery(id+"F0.wireOp",EDGE,"E3.24.0"),sQuery(id+"F0.wireOp",EDGE,"E3.24.1"),sQuery(id+"F0.wireOp",EDGE,"E3.25.0"),sQuery(id+"F0.wireOp",EDGE,"E3.25.1"),sQuery(id+"F0.wireOp",EDGE,"E3.26.0"),sQuery(id+"F0.wireOp",EDGE,"E3.26.1"),sQuery(id+"F0.wireOp",EDGE,"E3.27.0"),sQuery(id+"F0.wireOp",EDGE,"E3.27.1"),sQuery(id+"F0.wireOp",EDGE,"E3.28.0"),sQuery(id+"F0.wireOp",EDGE,"E3.28.1"),sQuery(id+"F0.wireOp",EDGE,"E3.29.0"),sQuery(id+"F0.wireOp",EDGE,"E3.29.1"),sQuery(id+"F0.wireOp",EDGE,"E3.30.0"),sQuery(id+"F0.wireOp",EDGE,"E3.30.1"),sQuery(id+"F0.wireOp",EDGE,"E3.31.0"),sQuery(id+"F0.wireOp",EDGE,"E3.31.1"),sQuery(id+"F0.wireOp",EDGE,"E3.32.0"),sQuery(id+"F0.wireOp",EDGE,"E3.32.1"),sQuery(id+"F0.wireOp",EDGE,"E3.33.0"),sQuery(id+"F0.wireOp",EDGE,"E3.33.1"),sQuery(id+"F0.wireOp",EDGE,"E3.34.0"),sQuery(id+"F0.wireOp",EDGE,"E3.34.1"),sQuery(id+"F0.wireOp",EDGE,"E3.35.0"),sQuery(id+"F0.wireOp",EDGE,"E3.35.1"),sQuery(id+"F0.wireOp",EDGE,"E3.36.0"),sQuery(id+"F0.wireOp",EDGE,"E3.36.1"),sQuery(id+"F0.wireOp",EDGE,"E3.37.0"),sQuery(id+"F0.wireOp",EDGE,"E3.37.1"),sQuery(id+"F0.wireOp",EDGE,"E3.38.0"),sQuery(id+"F0.wireOp",EDGE,"E3.38.1"),sQuery(id+"F0.wireOp",EDGE,"E3.39.0"),sQuery(id+"F0.wireOp",EDGE,"E3.39.1"),sQuery(id+"F0.wireOp",EDGE,"E3.40.0"),sQuery(id+"F0.wireOp",EDGE,"E3.40.1"),sQuery(id+"F0.wireOp",EDGE,"E3.41.0"),sQuery(id+"F0.wireOp",EDGE,"E3.41.1"),sQuery(id+"F0.wireOp",EDGE,"E3.42.0"),sQuery(id+"F0.wireOp",EDGE,"E3.42.1"),sQuery(id+"F0.wireOp",EDGE,"E3.43.0"),sQuery(id+"F0.wireOp",EDGE,"E3.43.1"),sQuery(id+"F0.wireOp",EDGE,"E3.44.0"),sQuery(id+"F0.wireOp",EDGE,"E3.44.1"),sQuery(id+"F0.wireOp",EDGE,"E3.45.0"),sQuery(id+"F0.wireOp",EDGE,"E3.45.1"),sQuery(id+"F0.wireOp",EDGE,"E3.46.0"),sQuery(id+"F0.wireOp",EDGE,"E3.46.1"),sQuery(id+"F0.wireOp",EDGE,"E3.47.0"),sQuery(id+"F0.wireOp",EDGE,"E3.47.1"),sQuery(id+"F0.wireOp",EDGE,"E4"),sQuery(id+"F0.wireOp",EDGE,"E5.1.0"),sQuery(id+"F0.wireOp",EDGE,"E5.2.0"),sQuery(id+"F0.wireOp",EDGE,"E5.3.0"),sQuery(id+"F0.wireOp",EDGE,"E5.4.0"),sQuery(id+"F0.wireOp",EDGE,"E5.5.0"),sQuery(id+"F0.wireOp",EDGE,"E5.6.0"),sQuery(id+"F0.wireOp",EDGE,"E5.7.0"),sQuery(id+"F0.wireOp",EDGE,"E5.8.0"),sQuery(id+"F0.wireOp",EDGE,"E5.9.0"),sQuery(id+"F0.wireOp",EDGE,"E5.10.0"),sQuery(id+"F0.wireOp",EDGE,"E5.11.0"),sQuery(id+"F0.wireOp",EDGE,"E5.12.0"),sQuery(id+"F0.wireOp",EDGE,"E5.13.0"),sQuery(id+"F0.wireOp",EDGE,"E5.14.0"),sQuery(id+"F0.wireOp",EDGE,"E5.15.0"),sQuery(id+"F0.wireOp",EDGE,"E5.16.0"),sQuery(id+"F0.wireOp",EDGE,"E5.17.0"),sQuery(id+"F0.wireOp",EDGE,"E5.18.0"),sQuery(id+"F0.wireOp",EDGE,"E5.19.0"),sQuery(id+"F0.wireOp",EDGE,"E5.20.0"),sQuery(id+"F0.wireOp",EDGE,"E5.21.0"),sQuery(id+"F0.wireOp",EDGE,"E5.22.0"),sQuery(id+"F0.wireOp",EDGE,"E5.23.0"),sQuery(id+"F0.wireOp",EDGE,"E5.24.0"),sQuery(id+"F0.wireOp",EDGE,"E5.25.0"),sQuery(id+"F0.wireOp",EDGE,"E5.26.0"),sQuery(id+"F0.wireOp",EDGE,"E5.27.0"),sQuery(id+"F0.wireOp",EDGE,"E5.28.0"),sQuery(id+"F0.wireOp",EDGE,"E5.29.0"),sQuery(id+"F0.wireOp",EDGE,"E5.30.0"),sQuery(id+"F0.wireOp",EDGE,"E5.31.0"),sQuery(id+"F0.wireOp",EDGE,"E5.32.0"),sQuery(id+"F0.wireOp",EDGE,"E5.33.0"),sQuery(id+"F0.wireOp",EDGE,"E5.34.0"),sQuery(id+"F0.wireOp",EDGE,"E5.35.0"),sQuery(id+"F0.wireOp",EDGE,"E5.36.0"),sQuery(id+"F0.wireOp",EDGE,"E5.37.0"),sQuery(id+"F0.wireOp",EDGE,"E5.38.0"),sQuery(id+"F0.wireOp",EDGE,"E5.39.0"),sQuery(id+"F0.wireOp",EDGE,"E5.40.0"),sQuery(id+"F0.wireOp",EDGE,"E5.41.0"),sQuery(id+"F0.wireOp",EDGE,"E5.42.0"),sQuery(id+"F0.wireOp",EDGE,"E5.43.0"),sQuery(id+"F0.wireOp",EDGE,"E5.44.0"),sQuery(id+"F0.wireOp",EDGE,"E5.45.0"),sQuery(id+"F0.wireOp",EDGE,"E5.46.0"),sQuery(id+"F0.wireOp",EDGE,"E5.47.0"),sQuery(id+"F0.wireOp",EDGE,"E6.filletArc"),sQuery(id+"F0.wireOp",EDGE,"E7.filletArc"),sQuery(id+"F0.wireOp",EDGE,"E8.filletArc"),sQuery(id+"F0.wireOp",EDGE,"E9.filletArc"),sQuery(id+"F0.wireOp",EDGE,"E10.filletArc"),sQuery(id+"F0.wireOp",EDGE,"E11.filletArc"),sQuery(id+"F0.wireOp",EDGE,"E12.filletArc"),sQuery(id+"F0.wireOp",EDGE,"E13.filletArc"),sQuery(id+"F0.wireOp",EDGE,"E14")])]});
            hole(context, id + "F3", {"style" : HoleStyle.SIMPLE, "endStyle" : HoleEndStyle.THROUGH, "holeDiameter" : 3 * mm, "locations" : qUnion([Q0, Q1, Q2, Q3]), "scope" : qUnion([Q4]), "isTappedThrough" : true});
        }
    });
